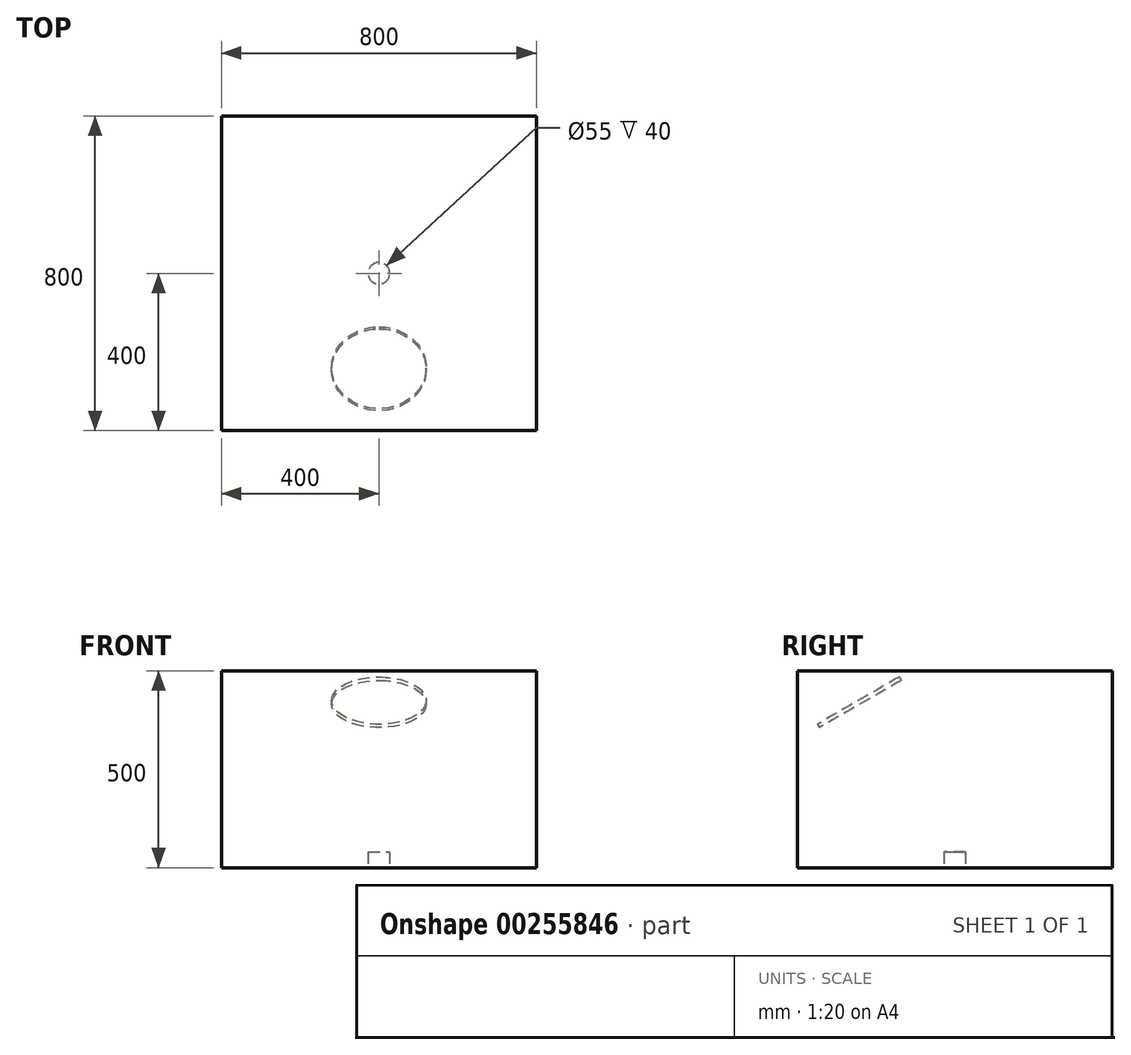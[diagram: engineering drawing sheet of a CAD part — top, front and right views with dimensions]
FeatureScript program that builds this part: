
annotation { "Feature Type Name" : "Feature", "Feature Type Description" : "" }
export const myFeature = defineFeature(function(context is Context, id is Id, definition is map)
    precondition{}
    {
        {
            var Q0;
            Q0=qCreatedBy(makeId("Top.planeOp"),FACE);
            var sketch = newSketch(context, id + "F0", { "sketchPlane" : qUnion([Q0])});
            skLineSegment(sketch, "E0.bottom", {"start": v(400, -400) * mm, "end": v(-400, -400) * mm});
            skLineSegment(sketch, "E0.top", {"start": v(400, 400) * mm, "end": v(-400, 400) * mm});
            skLineSegment(sketch, "E0.left", {"start": v(400, -400) * mm, "end": v(400, 400) * mm});
            skLineSegment(sketch, "E0.right", {"start": v(-400, -400) * mm, "end": v(-400, 400) * mm});
            skPoint(sketch, "E0.middle", {"position": v(0, 0) * mm});
            skSolve(sketch);
        }
        {
            var Q0;
            Q0=makeQuery(id+"F0.imprint","IMPRINT",FACE,{"disambiguationData":[TD([[makeQuery(id+"F0.imprint","IMPRINT",EDGE,{"derivedFrom":sQuery(id+"F0.wireOp",EDGE,"E0.bottom")}),-1.0]])]});
            extrude(context, id + "F1", {"entities" : qUnion([Q0]), "depth" : 500 * mm});
        }
        {
            var Q0;
            Q0=makeQuery(id+"F1.opExtrude","CAP_FACE",FACE,{"disambiguationData":[OSD([sQuery(id+"F0.wireOp",EDGE,"E0.bottom"),sQuery(id+"F0.wireOp",EDGE,"E0.top"),sQuery(id+"F0.wireOp",EDGE,"E0.left"),sQuery(id+"F0.wireOp",EDGE,"E0.right")])],"isStart":true});
            var sketch = newSketch(context, id + "F2", { "sketchPlane" : qUnion([Q0])});
            skCircle(sketch, "E1", {"center": v(0, 0) * mm, "radius": 27.5 * mm});
            skSolve(sketch);
        }
        {
            var Q0;
            Q0=makeQuery(id+"F2.imprint","IMPRINT",FACE,{"disambiguationData":[TD([[makeQuery(id+"F2.imprint","IMPRINT",EDGE,{"derivedFrom":sQuery(id+"F2.wireOp",EDGE,"E1")}),1.0]])]});
            extrude(context, id + "F3", {"entities" : qUnion([Q0]), "operationType" : NewBodyOperationType.REMOVE, "oppositeDirection" : true, "depth" : 40 * mm});
        }
        {
            var Q0;
            Q0=qCreatedBy(makeId("Top.planeOp"),FACE);
            var sketch = newSketch(context, id + "F4", { "sketchPlane" : qUnion([Q0])});
            skLineSegment(sketch, "E2", {"start": v(-63.72, 0) * mm, "end": v(70.67, 0) * mm});
            skSolve(sketch);
        }
        {
            var Q0;
            Q0=qCreatedBy(makeId("Front.planeOp"),FACE);
            var Q1;
            Q1=sQuery(id+"F4.wireOp",EDGE,"E2");
            cPlane(context, id + "F5", {"entities" : qUnion([Q0, Q1]), "cplaneType" : CPlaneType.LINE_ANGLE, "offset" : 25 * mm, "angle" : 60 * degree, "oppositeDirection" : true, "width" : 150 * mm, "height" : 150 * mm});
        }
        {
            var Q0;
            Q0=qCreatedBy(id+"F5.planeOp",FACE);
            cPlane(context, id + "F6", {"entities" : qUnion([Q0]), "cplaneType" : CPlaneType.OFFSET, "offset" : 480 * mm, "oppositeDirection" : true, "width" : 150 * mm, "height" : 150 * mm});
        }
        {
            var Q0;
            Q0=qCreatedBy(id+"F6.planeOp",FACE);
            var sketch = newSketch(context, id + "F7", { "sketchPlane" : qUnion([Q0])});
            skCircle(sketch, "E3", {"center": v(0, 0) * mm, "radius": 120 * mm});
            skSolve(sketch);
        }
        {
            var Q0;
            Q0=makeQuery(id+"F7.imprint","IMPRINT",FACE,{"disambiguationData":[TD([[makeQuery(id+"F7.imprint","IMPRINT",EDGE,{"derivedFrom":sQuery(id+"F7.wireOp",EDGE,"E3")}),1.0]])]});
            extrude(context, id + "F8", {"entities" : qUnion([Q0]), "operationType" : NewBodyOperationType.REMOVE, "oppositeDirection" : true, "depth" : 10 * mm});
        }
    });
